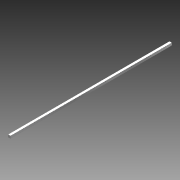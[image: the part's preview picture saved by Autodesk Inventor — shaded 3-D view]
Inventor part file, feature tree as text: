
AUTODESK INVENTOR PART (.ipt)
format: ipt  version: 2012 (Build 160160000, 160)  size: 131,584 bytes
history: native  units: in
note: dims shown in document units (in); Inventor stores cm internally (conversion verified against a paired STEP export)
features: other x2, imported_body x1, plane x1, split x1, sketch x1
ambient origin geometry x8: Origin, YZ Plane, XZ Plane, XY Plane, X Axis, Y Axis, Z Axis, Center Point
feature tree (6):
  parser-record x1  (decoder bookkeeping rows leaked as tree rows — omitted from the tree; the rows remain in map.json)
  imported_body  "Base1"
  plane  "Work Plane1"
  split  "Split1"
  sketch  "Sketch1"  dims[d0=-4.0in]
  other  "Work Axis1"
